# Revit family: AnchorPoint_Kattsafe_ThroughBolt
name_source: partatom
category: Specialty Equipment
units: mm (PartAtom-declared; Revit-internal decimal feet)

## family parameters
Cut with Voids When Loaded = Yes
Enable Cutting in Views = No
Host = Face
Maintain Annotation Orientation = No
OmniClass Number = 23.27.71.21
Part Type = Normal
Room Calculation Point = No
Round Connector Dimension = Use Diameter
Shared = No

## types (1)
- Type 1
    Assembly Code = E1090100
    Default Elevation = 0 mm  [stored 0 ft]
    Description = Our Kattsafe anchor points are specifically designed, manufactured, and tested to comply with and often exceed Australian Standards, effectively handling excessive loads and saving lives when using a harness and lanyard system.
    ElementType = Fall Protection
    Export Type to IFC As = IfcBuildingElementProxy
    IfcExportAs = IfcBuildingElementProxy
    IfcExportType = USERDEFINED
    Manufacturer = Kattsafe®
    ManufacturerOverallDepth = 70 mm  [stored 0.229659 ft]
    ManufacturerOverallWidth = 70 mm  [stored 0.229659 ft]
    ManufacturerSpecCode = AP124
    ManufacturerURLProductSpecific = https://kattsafe.com.au
    Material = Steel_Stainless_Kattsafe_Satin
    Model = AP124
    ModifiedIssue = 20240430 $
    Type Comments = Through Bolt Anchor - 15kN rated - 0.7kg
    Type IFC Predefined Type = USERDEFINED
    URL = https://kattsafe.com.au
    Uniclass2015Code = Pr_40_70_75_75
    Uniclass2015Title = Safety access anchor devices
    Uniclass2015Version = Products v1.23

note: [stored X ft] marks values corroborated as IEEE doubles in the binary element streams (Revit-internal decimal feet)

## geometry (parser evidence)
native form markers: Sweep x3
no freeform markers — native parametric forms only
